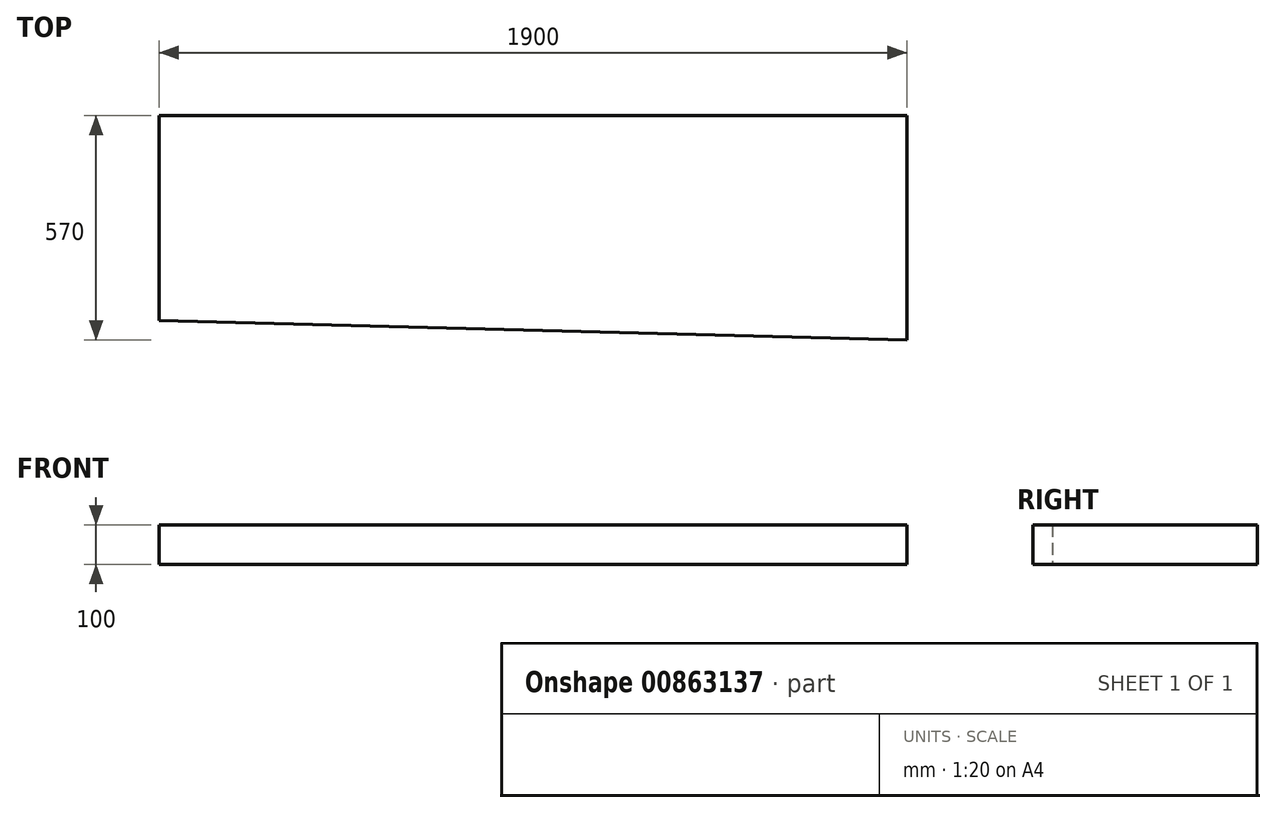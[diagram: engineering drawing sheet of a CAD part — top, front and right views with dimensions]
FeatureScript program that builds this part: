
annotation { "Feature Type Name" : "Feature", "Feature Type Description" : "" }
export const myFeature = defineFeature(function(context is Context, id is Id, definition is map)
    precondition{}
    {
        {
            var Q0;
            Q0=qCreatedBy(makeId("Top.planeOp"),FACE);
            var sketch = newSketch(context, id + "F0", { "sketchPlane" : qUnion([Q0])});
            skLineSegment(sketch, "E0", {"start": v(0, 0) * mm, "end": v(0, 520) * mm});
            skLineSegment(sketch, "E1", {"start": v(0, 520) * mm, "end": v(1900, 520) * mm});
            skLineSegment(sketch, "E2", {"start": v(1900, 520) * mm, "end": v(1900, -50) * mm});
            skLineSegment(sketch, "E3", {"start": v(1900, -50) * mm, "end": v(0, 0) * mm});
            skSolve(sketch);
        }
        {
            var Q0;
            Q0=makeQuery(id+"F0.imprint","IMPRINT",FACE,{"disambiguationData":[TD([[makeQuery(id+"F0.imprint","IMPRINT",EDGE,{"derivedFrom":sQuery(id+"F0.wireOp",EDGE,"E0")}),-1.0]])]});
            extrude(context, id + "F1", {"entities" : qUnion([Q0]), "depth" : 100 * mm, "offsetDistance" : 25 * mm});
        }
    });
